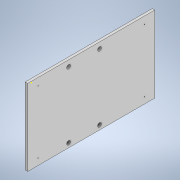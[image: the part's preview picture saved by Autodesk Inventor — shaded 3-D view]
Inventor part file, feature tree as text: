
AUTODESK INVENTOR PART (.ipt)
format: ipt  version: 2020 (Build 240168000, 168)  size: 111,616 bytes
history: native  units: in
note: dims shown in document units (in); Inventor stores cm internally (conversion verified against a paired STEP export)
features: sketch x4, hole x2, extrude x1
ambient origin geometry x8: Origin, YZ Plane, XZ Plane, XY Plane, X Axis, Y Axis, Z Axis, Center Point
bodies: Solid1 (feature_tree)
feature tree (7):
  extrude  "Extrusion1"  Depth=19.685in
  hole  "Hole1"  [1 undecoded]
  sketch  "Sketch4"  dims[d4=0.1181in d5=0.75in d6=0.375in d7=0.25in d8=0.5635in d9=1.0in d10=0.8108in]
  hole  "Hole7"  [1 undecoded]
  sketch  "Sketch1"  dims[d0=11.811in d1=19.685in]
  sketch  "Sketch2"  dims[d2=0.3937in d3=0.0in]
  sketch  "Sketch9"  dims[d48=0.5906in d49=0.75in d50=0.375in d51=0.25in d52=0.5635in d53=1.0in d54=0.8108in d34=1.0in d35=1.0in d36=1.0in d37=0.15in d38=0.5906in d39=0.375in d40=0.5635in d41=0.75in d42=0.8108in d43=0.0625in d44=0.75in d45=0.375in d46=0.375in d47=0.5635in d55=0.75in d56=0.8108in d57=0.0625in d58=0.75in d59=0.375in]
note: 2 required parameter values undecoded (feature->parameter linkage not recoverable at this tier; creation-order binding heuristic only, values carry confidence <= 0.55)
